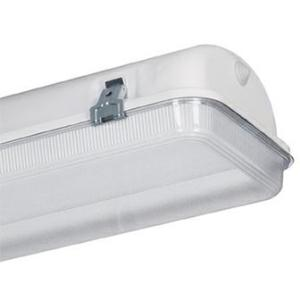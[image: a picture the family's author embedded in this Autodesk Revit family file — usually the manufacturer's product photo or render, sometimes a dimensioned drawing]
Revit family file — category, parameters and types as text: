
# Revit family: 3f_filippi_-_beta_i3f_75_pc_ampio_3f_filippi_-_55607_-_i3f_led_752x12w_ep_ampio_l655
name_source: partatom
category: Lighting Fixtures
units: mm (PartAtom-declared; Revit-internal decimal feet)

## family parameters
Cut with Voids When Loaded = No
Host = Face
Light Source = No
Part Type = Normal
Room Calculation Point = No
Round Connector Dimension = Use Diameter
Shared = No

## types (1)
- 3F Filippi - Beta i3F 75 PC Ampio (1 x LED, 3955 lm, 29 W, 4000 K)
    Apparent Load = 29 VA
    Approval mark = ENEC
    CIE Flux Codes = 52 82 96 97 100
    Color Rendering = 80
    Color Temperature = 4000 K
    Control Gear = Electronic ballast
    Default Elevation = 1800 mm
    Description = ILLUMINOTECHNICAL
Luminous efficiency 100% (DLOR 97%, ULOR 3%).
Initial luminous flux of the luminaire 3955 lm.
Emergency luminaire luminous flux BLF 14.3%.
Wide symmetric distribution.
Installation Interdistance Transv.D = 1.27 x hu - Long.D = 1.26 x hu.
Tabular UGR (CIE 117 - 4H-8H; S=0.25H; 70/50/20): RUG 20.5 - 22.1.
Beam angle: 92° - 100°.
Luminous efficacy 136 lm/W.
Lifetime (L93/B10): 30000 h. (tq+25°C)
Lifetime (L90/B10): 50000 h. (tq+25°C)
Lifetime (L85/B10): 80000 h. (tq+25°C)
Lifetime (L80/B10): 100000 h. (tq+25°C)
Sudden decreased luminous flux after 50000 hours: 0% (C0).
Photobiological safety in compliance with IEC/TR 62778: RG0 risk exempt, (IEC 62471).
In compliance with IEC/EN 62722-2-1 - IEC/EN 62717 standards.

SOURCE
2 linear LED modules 12W/840.
Energy efficiency class (UE 2019/2020 - UE 2019/2015): D.
CIE 13.3 Colour rendering index: CRI >80 (R9 <50%).
IES TM-30 Fidelity Index: Rf = 84 Rg = 95.
CCT nominal colour temperature 4000 K.
Colour initial tolerance (MacAdam): SDCM 3.

MECHANICAL
Single-piece housing in pressed steel, powder-coated in white epoxy-polyester.
Diffuser in self-extinguishing V2 polycarbonate, photo-engraved interior, UV stabilised, injection moulded, with smooth outer surface, sealing gasket, hinged opening by means of galvanised steel clips.
Wide flow recuperator, oversized, in specular aluminium with superficial titanium-magnesium treatment, non-iridescent.
Gear-tray unit in hot-galvanised steel, painted in white polyester, fixed to the housing by means of "Ribloc" rapid devices in galvanised steel, hinged opening.
Luminaire with limited surface temperature. - D - (EN 60598-2-24)
Dimensions: 655x235 mm, height 140 mm. Weight 4.311 kg.
IP65 protection degree.
Mechanical strength to impacts IK10 (20 joule).
Glow-wire test resistance 850°C.

ELECTRICAL
Halogen Free electronic wiring 230V-50/60Hz, power factor 0.85, THD <25%, constant output current, SELV, class I, 1 driver.
Power of the luminaire 29 W.
CE - IEC 60598-1 - EN 60598-1.
EP maintained emergency wiring on board, 1h duration, 24h recharge; compliant with EN 60598-2-22, excluding high risk areas.
SAFE FLICKER: PstLM=<1 and SVM=<0.4 (IEC TR 61547-1 and IEC TR 63158), to ensure a more comfortable and safe light.
Ambient temperature from +5°C to +25°C.
Temperature class T6 max 85°C.
Relative humidity UR: <85%.

INSTALLATION
Ceiling / Suspended / Wall.
All accessories dedicated to this product are available on the Catalog and on our website www.3F-Filippi.com.

APPLICATIONS
Suitable product for food production plants (HACCP), IFS (Food Version 6), BRC (GSFS Food Version 7).
In industrial environments, stores and dry, dusty indoor environments, subject to occasional water splashes.

WARNING
Fixture not suitable for cold stores with an ambient temperature <5°C and/or relative humidity >85%.
Luminaire designed for disposal/recycling at end-of-life.
Replaceable (LED only) light source by a professional. Replaceable control gear by a professional.
    Height = 140 mm  [stored 0.459318 ft]
    Lamp = 1 x LED
    Lamp Light Flux = 3955 lm
    Lamp Power = 29 W
    Lamp count = 1
    Length = 655 mm
    Lifetime = 50000 h
    Luminous efficacy = 136 lm/W
    Manufacturer = 3F Filippi
    ModVariant = No
    Model = 3F Filippi - 55607 - i3F LED 752x12W EP AMPIO L655
    Mounting Place = Ceiling
    Mounting Type = Pendant
    Number of Poles = 1
    OnlyDefault = Yes
    Power Factor = 1
    Product Name = 3F Filippi - Beta i3F 75 PC Ampio
    Product group = pendant luminaire
    ProductGroupID = 9
    Protection Class = Protection class I
    Protection Degree = IP 65
    RLX_Detail_Level = 1
    RLX_Emergency_Light_Flux = 0 lm
    RLX_Emergency_Type = 0
    RLX_Emergency_Type_DB = No
    RlxData = <blob elided: 65401 chars, md5=fc228522>
    Socket = socket
    Standby Power = 0 W
    System Light Flux = 3955 lm
    System Power = 29 W
    Type Comments = Product without accessories
    Type Image = 3ffilippi_55607.jpg
    URL = http://relux.com
    VarID = ---
    Voltage = 0 V
    Weight = 0.00 kg
    Width = 235 mm

note: [stored X ft] marks values corroborated as IEEE doubles in the binary element streams (Revit-internal decimal feet)

## geometry (parser evidence)
native form markers: Blend x4, Sweep x10
no freeform markers — native parametric forms only
